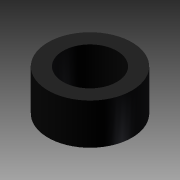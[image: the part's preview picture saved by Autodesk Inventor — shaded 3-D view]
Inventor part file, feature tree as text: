
AUTODESK INVENTOR PART (.ipt)
format: ipt  version: 2012 (Build 160160000, 160)  size: 75,264 bytes
history: native  units: mm
features: extrude x1, sketch x1
ambient origin geometry x8: Origin, YZ Plane, XZ Plane, XY Plane, X Axis, Y Axis, Z Axis, Center Point
bodies: Solid1 (feature_tree)
feature tree (2):
  extrude  "Extrusion1"  Depth=7.5mm
  sketch  "Sketch1"  dims[d0=42.0mm d1=7.5mm d2=20.5mm d3=0.0mm]
